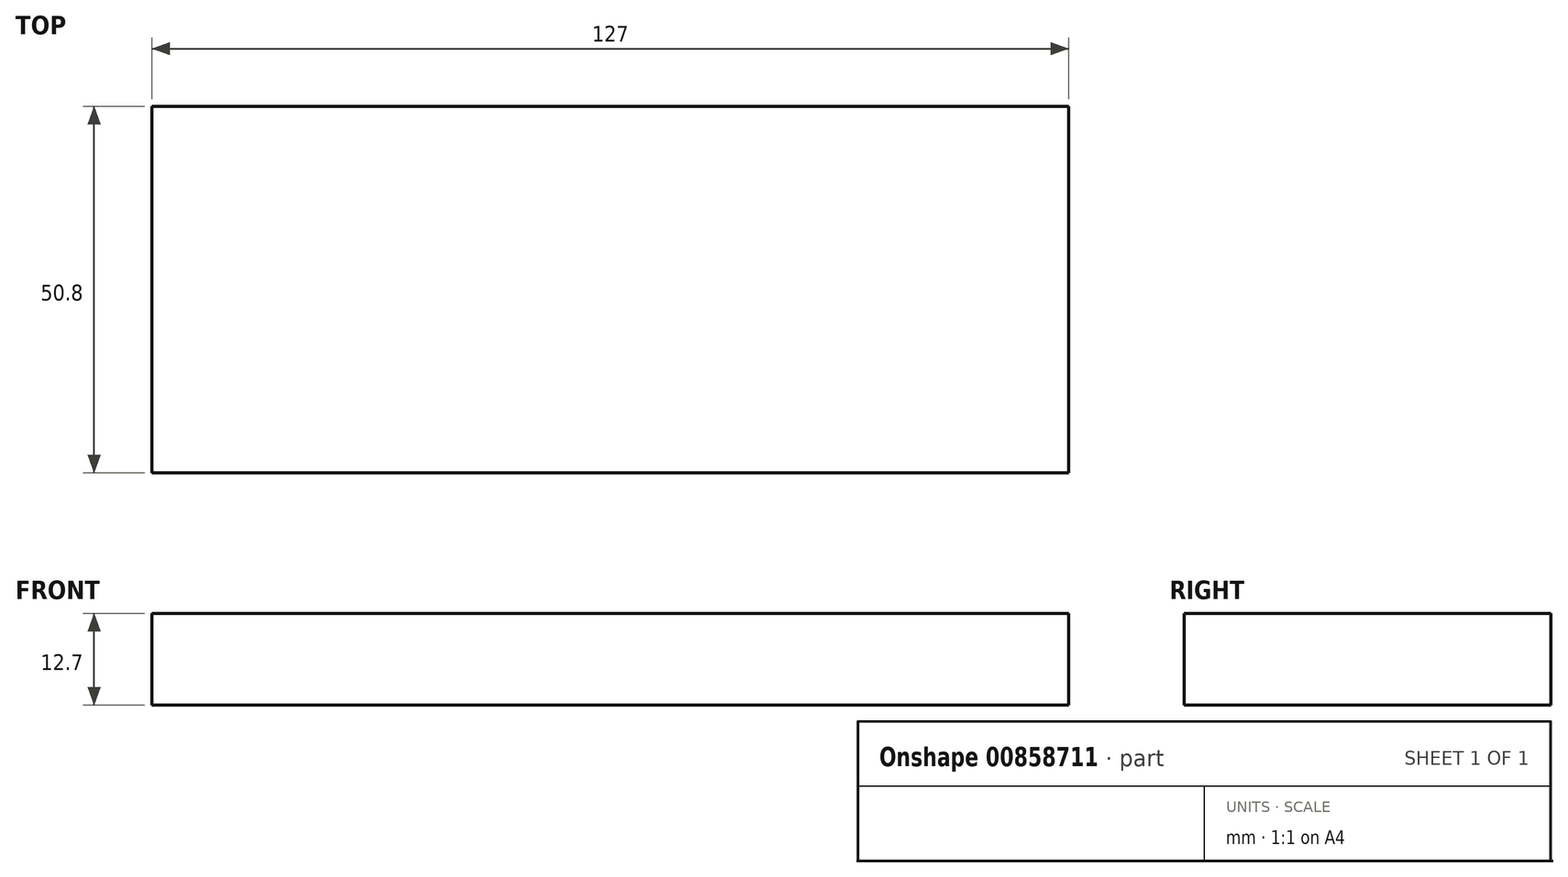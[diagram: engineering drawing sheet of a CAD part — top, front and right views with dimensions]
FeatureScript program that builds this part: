
annotation { "Feature Type Name" : "Feature", "Feature Type Description" : "" }
export const myFeature = defineFeature(function(context is Context, id is Id, definition is map)
    precondition{}
    {
        {
            var Q0;
            Q0=qCreatedBy(makeId("Top.planeOp"),FACE);
            var sketch = newSketch(context, id + "F0", { "sketchPlane" : qUnion([Q0])});
            skLineSegment(sketch, "E0.bottom", {"start": v(-82.42, 13.3) * mm, "end": v(44.58, 13.3) * mm});
            skLineSegment(sketch, "E0.top", {"start": v(-82.42, -37.5) * mm, "end": v(44.58, -37.5) * mm});
            skLineSegment(sketch, "E0.left", {"start": v(-82.42, 13.3) * mm, "end": v(-82.42, -37.5) * mm});
            skLineSegment(sketch, "E0.right", {"start": v(44.58, 13.3) * mm, "end": v(44.58, -37.5) * mm});
            skSolve(sketch);
        }
        {
            var Q0;
            Q0=makeQuery(id+"F0.imprint","IMPRINT",FACE,{"disambiguationData":[TD([[makeQuery(id+"F0.imprint","IMPRINT",EDGE,{"derivedFrom":sQuery(id+"F0.wireOp",EDGE,"E0.bottom")}),-1.0]])]});
            extrude(context, id + "F1", {"entities" : qUnion([Q0]), "depth" : 12.7 * mm, "offsetDistance" : 25.4 * mm});
        }
    });
